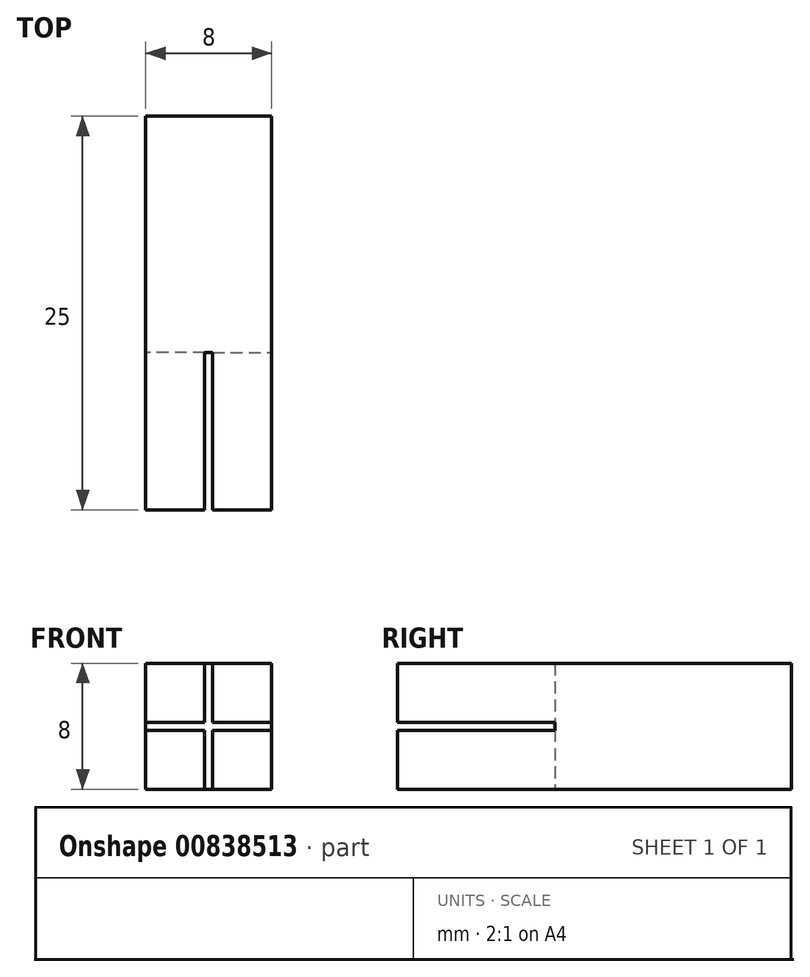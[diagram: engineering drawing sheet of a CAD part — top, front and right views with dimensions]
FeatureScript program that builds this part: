
annotation { "Feature Type Name" : "Feature", "Feature Type Description" : "" }
export const myFeature = defineFeature(function(context is Context, id is Id, definition is map)
    precondition{}
    {
        {
            var Q0;
            Q0=qCreatedBy(makeId("Front.planeOp"),FACE);
            var sketch = newSketch(context, id + "F0", { "sketchPlane" : qUnion([Q0])});
            skLineSegment(sketch, "E0.bottom", {"start": v(-2.66, 1.27) * mm, "end": v(5.34, 1.27) * mm});
            skLineSegment(sketch, "E0.top", {"start": v(-2.66, -6.73) * mm, "end": v(5.34, -6.73) * mm});
            skLineSegment(sketch, "E0.left", {"start": v(-2.66, 1.27) * mm, "end": v(-2.66, -6.73) * mm});
            skLineSegment(sketch, "E0.right", {"start": v(5.34, 1.27) * mm, "end": v(5.34, -6.73) * mm});
            skSolve(sketch);
        }
        {
            var Q0;
            Q0 = qSketchRegion(id + "F0", true);
            extrude(context, id + "F1", {"entities" : qUnion([Q0]), "depth" : 25 * mm, "offsetDistance" : 25.4 * mm});
        }
        {
            var Q0;
            Q0=makeQuery(id+"F1.opExtrude","CAP_FACE",FACE,{"disambiguationData":[OSD([sQuery(id+"F0.wireOp",EDGE,"E0.bottom"),sQuery(id+"F0.wireOp",EDGE,"E0.top"),sQuery(id+"F0.wireOp",EDGE,"E0.left"),sQuery(id+"F0.wireOp",EDGE,"E0.right")])],"isStart":false});
            var sketch = newSketch(context, id + "F2", { "sketchPlane" : qUnion([Q0])});
            skLineSegment(sketch, "E1", {"start": v(1.09, 1.27) * mm, "end": v(1.09, -2.48) * mm});
            skLineSegment(sketch, "E2", {"start": v(1.59, 1.27) * mm, "end": v(1.59, -2.48) * mm});
            skLineSegment(sketch, "E3", {"start": v(5.34, -2.48) * mm, "end": v(1.59, -2.48) * mm});
            skLineSegment(sketch, "E4", {"start": v(-2.66, -2.98) * mm, "end": v(1.09, -2.98) * mm});
            skPoint(sketch, "E5.orphan", {"position": v(1.34, 1.27) * mm});
            skPoint(sketch, "E6.start.orphan", {"position": v(-2.66, -2.73) * mm});
            skLineSegment(sketch, "E7.trimOffspring", {"start": v(1.09, -2.98) * mm, "end": v(1.09, -6.73) * mm});
            skLineSegment(sketch, "E8.trimOffspring", {"start": v(1.59, -2.98) * mm, "end": v(1.59, -6.73) * mm});
            skPoint(sketch, "E9.trimOffspring.end.orphan", {"position": v(5.34, -2.73) * mm});
            skLineSegment(sketch, "E10.trimOffspring", {"start": v(1.59, -2.98) * mm, "end": v(5.34, -2.98) * mm});
            skPoint(sketch, "E11.end.orphan", {"position": v(1.34, -6.73) * mm});
            skLineSegment(sketch, "E12.trimOffspring", {"start": v(1.09, -2.48) * mm, "end": v(-2.66, -2.48) * mm});
            skLineSegment(sketch, "E13", {"start": v(1.09, 1.27) * mm, "end": v(1.59, 1.27) * mm});
            skLineSegment(sketch, "E14", {"start": v(5.34, -2.48) * mm, "end": v(5.34, -2.98) * mm});
            skLineSegment(sketch, "E15", {"start": v(1.09, -6.73) * mm, "end": v(1.59, -6.73) * mm});
            skLineSegment(sketch, "E16", {"start": v(-2.66, -2.98) * mm, "end": v(-2.66, -2.48) * mm});
            skSolve(sketch);
        }
        {
            var Q0;
            Q0 = qSketchRegion(id + "F2", true);
            extrude(context, id + "F3", {"entities" : qUnion([Q0]), "operationType" : NewBodyOperationType.REMOVE, "oppositeDirection" : true, "depth" : 10 * mm, "offsetDistance" : 25.4 * mm});
        }
    });
